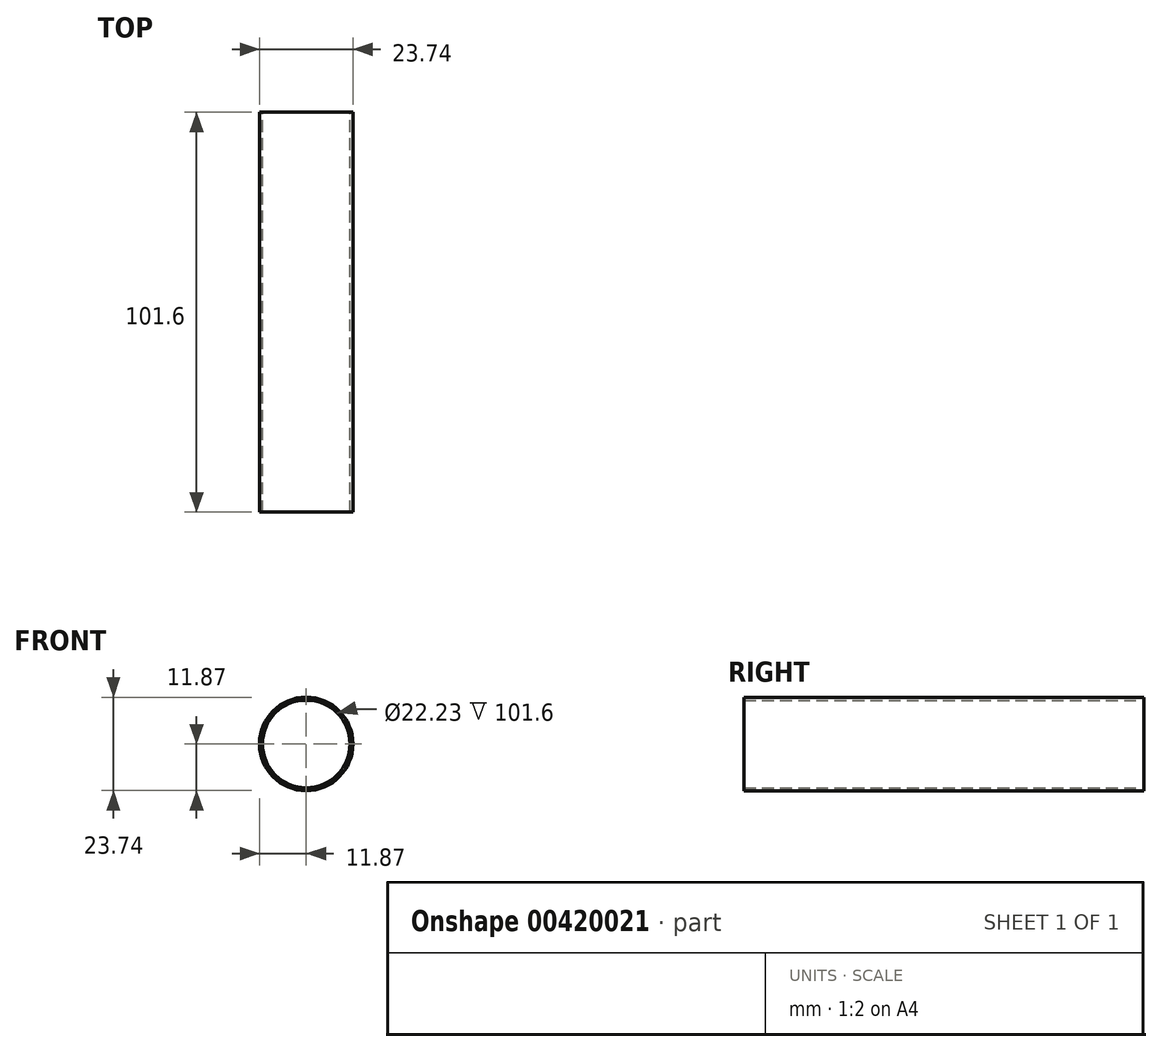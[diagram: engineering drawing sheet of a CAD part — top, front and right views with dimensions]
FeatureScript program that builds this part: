
annotation { "Feature Type Name" : "Feature", "Feature Type Description" : "" }
export const myFeature = defineFeature(function(context is Context, id is Id, definition is map)
    precondition{}
    {
        {
            var Q0;
            Q0=qCreatedBy(makeId("Front.planeOp"),FACE);
            var sketch = newSketch(context, id + "F0", { "sketchPlane" : qUnion([Q0])});
            skCircle(sketch, "E0", {"center": v(0, 0) * mm, "radius": 11.87 * mm});
            skCircle(sketch, "E1", {"center": v(0, 0) * mm, "radius": 11.11 * mm});
            skSolve(sketch);
        }
        {
            var Q0;
            Q0 = qSketchRegion(id + "F0", true);
            extrude(context, id + "F1", {"entities" : qUnion([Q0]), "depth" : 101.6 * mm});
        }
    });
